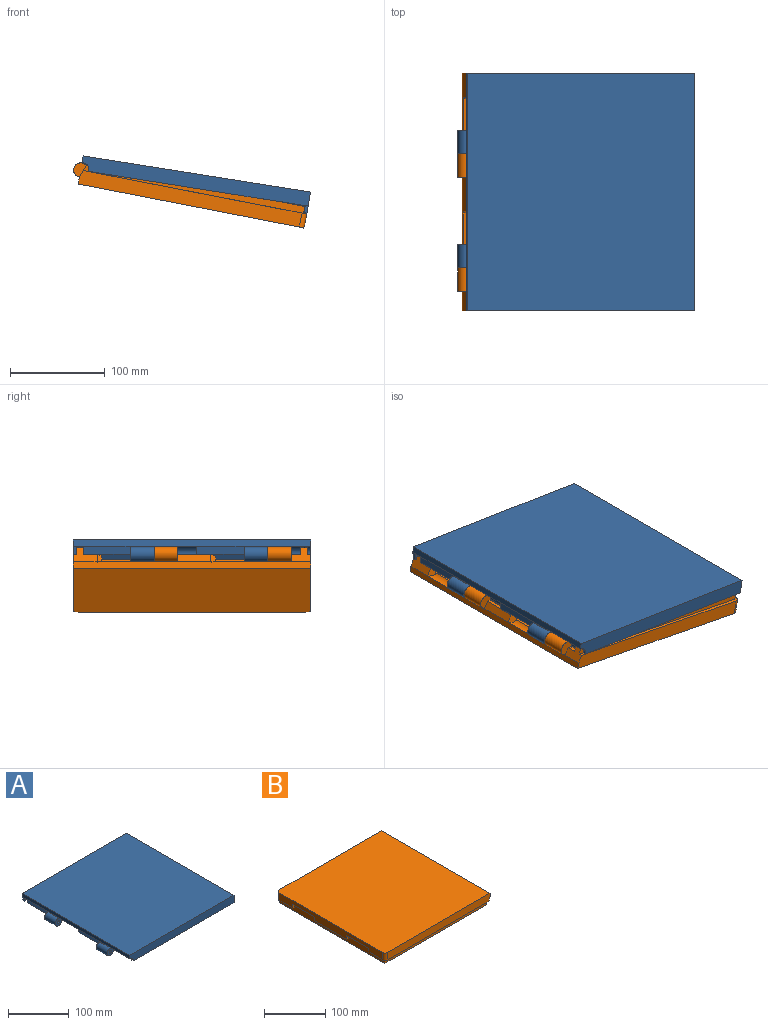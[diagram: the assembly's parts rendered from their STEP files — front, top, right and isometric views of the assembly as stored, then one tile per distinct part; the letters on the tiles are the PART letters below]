
ASSEMBLY  parts=2 mates=1
PART A: 51 faces, bbox 250x250x22.5 mm
  f0: plane 239.84x37.5mm, normal (0,0,-1), area 914.4mm2, adj f9,f12,f14,f18,f19,f49
  f1: plane 75x2.9mm, normal (0,0,-1), area 217.5mm2, adj f12,f18,f43,f50
  f2: plane 228.8x228.74mm, normal (0,0,-1), area 51620.4mm2, adj f3,f6,f8,f16,f19,f20,f21,f23
  f3: plane 70x8.5mm, normal (-0.95,0,-0.3), area 466.4mm2, adj f2,f10,f21,f23,f25,f30
  f4: plane 234x37.5mm, normal (0,0,-1), area 894.5mm2, adj f11,f12,f15,f18,f20,f44
  f5: plane 227.28x7.2mm, normal (0,0,-1), area 1636.4mm2, adj f8,f15,f16,f20
  f6: plane 231.09x7.5mm, normal (0,1,0), area 1724.1mm2, adj f2,f7,f16,f19
  f7: plane 230.97x7.2mm, normal (0,0,-1), area 1663mm2, adj f6,f14,f16,f19
  f8: plane 227.4x7.5mm, normal (0,-1,0), area 1681.2mm2, adj f2,f5,f16,f20
  f9: plane 242.5x15mm, normal (0,1,0), area 3626.2mm2, adj f0,f10,f12,f13,f19
  f10: plane 250x6.5mm, normal (-1,0,0), area 1625mm2, adj f3,f9,f11,f13,f19,f20,f31
  f11: plane 242.5x15mm, normal (0,-1,0), area 3580.8mm2, adj f4,f10,f12,f13,f20
  f12: plane 250x22.5mm, normal (1,0,0), area 4500mm2, adj f0,f1,f4,f9,f11,f13,f41,f43
  f13: plane 250x242.5mm, normal (0,0,1), area 60625mm2, adj f9,f10,f11,f12
  f14: plane 239.29x8mm, normal (0,-1,0), area 1789.7mm2, adj f0,f7,f16,f17,f18,f19
  f15: plane 235.6x8mm, normal (0,1,0), area 1746.8mm2, adj f4,f5,f16,f17,f18,f20
  f16: cylinder r=231.4mm len=243.2mm, axis (0,-1,0), area 1838mm2, adj f2,f5,f6,f7,f8,f14,f15,f17
  f17: plane 243.2x8.2mm, normal (0,0,-1), area 1995.4mm2, adj f14,f15,f16,f18
  f18: cylinder r=239.6mm len=243.2mm, axis (0,-1,0), area 1946mm2, adj f0,f1,f4,f14,f15,f17,f45,f48
  f19: plane 80x8.5mm, normal (-0.95,0,-0.3), area 498.8mm2, adj f0,f2,f6,f7,f9,f10,f14,f32
  f20: cylinder r=8.5mm len=50mm, axis (0,-1,0), area 601.4mm2, adj f2,f4,f5,f8,f10,f11,f15,f21
  f21: plane 8.5x8.5mm, normal (0,-1,0), area 12.4mm2, adj f2,f3,f20,f25
  f22: plane 5.4x5.4mm, normal (0,-1,0), area 22.7mm2, adj f24,f28,f29
  f23: plane 15x15mm, normal (0,1,0), area 143.7mm2, adj f2,f3,f25
  f24: cylinder r=2.7mm len=20mm, axis (0,1,0), area 312.8mm2, adj f22,f26,f27,f28,f29
  f25: cylinder r=7.5mm len=25mm, axis (0,1,0), area 948.8mm2, adj f2,f3,f21,f23,f26
  f26: plane 15x15mm, normal (0,-1,0), area 153.8mm2, adj f24,f25
  f27: plane 1.64x0.56mm, normal (0,-1,0), area 0.2mm2, adj f24,f28,f29
  f28: plane 15x1.64mm, normal (-0.95,0,-0.3), area 25.8mm2, adj f22,f24,f27,f29
  f29: plane 15x0.04mm, normal (0,0,-1), area 0.7mm2, adj f22,f24,f27,f28
  f30: plane 8.5x8.5mm, normal (0,1,0), area 45.5mm2, adj f2,f3,f31
  f31: cylinder r=8.5mm len=50mm, axis (0,-1,0), area 667.6mm2, adj f2,f10,f30,f32
  f32: plane 8.5x8.5mm, normal (0,-1,0), area 12.4mm2, adj f2,f19,f31,f36
  f33: plane 5.4x5.4mm, normal (0,-1,0), area 22.7mm2, adj f35,f39,f40
  f34: plane 15x15mm, normal (0,1,0), area 143.7mm2, adj f2,f19,f36
  f35: cylinder r=2.7mm len=20mm, axis (0,1,0), area 312.8mm2, adj f33,f37,f38,f39,f40
  f36: cylinder r=7.5mm len=25mm, axis (0,1,0), area 948.8mm2, adj f2,f19,f32,f34,f37
  f37: plane 15x15mm, normal (0,-1,0), area 153.8mm2, adj f35,f36
  f38: plane 1.64x0.56mm, normal (0,-1,0), area 0.2mm2, adj f35,f39,f40
  f39: plane 15x1.64mm, normal (-0.95,0,-0.3), area 25.8mm2, adj f33,f35,f38,f40
  f40: plane 15x0.04mm, normal (0,0,-1), area 0.7mm2, adj f33,f35,f38,f39
  f41: plane 50x3.03mm, normal (0,0,-1), area 151.7mm2, adj f12,f42,f43,f44
  f42: plane 50x7.5mm, normal (-1,0,0), area 375mm2, adj f41,f43,f44,f45
  f43: plane 7.5x3.03mm, normal (0,1,0), area 22.8mm2, adj f1,f12,f41,f42,f45
  f44: plane 7.5x3.03mm, normal (0,-1,0), area 22.8mm2, adj f4,f12,f41,f42,f45
  f45: plane 50x0.13mm, normal (0,0,1), area 6.7mm2, adj f18,f42,f43,f44
  f46: plane 50x3.03mm, normal (0,0,-1), area 151.7mm2, adj f12,f47,f49,f50
  f47: plane 50x7.5mm, normal (-1,0,0), area 375mm2, adj f46,f48,f49,f50
  f48: plane 50x0.13mm, normal (0,0,1), area 6.7mm2, adj f18,f47,f49,f50
  f49: plane 7.5x3.03mm, normal (0,1,0), area 22.8mm2, adj f0,f12,f46,f47,f48
  f50: plane 7.5x3.03mm, normal (0,-1,0), area 22.8mm2, adj f1,f12,f46,f47,f48
PART B: 51 faces, bbox 250x250x22.5 mm
  f0: plane 74x3.5mm, normal (0,0,-1), area 259mm2, adj f12,f15,f46,f48
  f1: plane 239.84x37mm, normal (0,0,-1), area 951.3mm2, adj f7,f9,f12,f15,f26,f43,f45
  f2: plane 236x8mm, normal (-1,0,0), area 1171.5mm2, adj f3,f5,f17,f19,f20,f21,f23,f24
  f3: plane 39.15x4.34mm, normal (0,0,-1), area 161mm2, adj f2,f4,f34,f38
  f4: plane 60x8.5mm, normal (0.95,0,-0.3), area 338.1mm2, adj f3,f13,f34,f35,f38,f39
  f5: plane 9.5x4.34mm, normal (0,0,-1), area 41.3mm2, adj f2,f6,f24,f30
  f6: plane 45x16mm, normal (0.95,0,-0.3), area 259.5mm2, adj f5,f8,f10,f11,f13,f16,f24,f27
  f7: plane 237.5x15mm, normal (0,1,0), area 3551.2mm2, adj f1,f13,f14,f26,f43
  f8: plane 237.5x15mm, normal (0,-1,0), area 3551.2mm2, adj f6,f11,f13,f14,f44
  f9: plane 236.34x7.5mm, normal (0,1,0), area 1763.8mm2, adj f1,f10,f15,f26
  f10: plane 243x234mm, normal (0,0,-1), area 4879mm2, adj f6,f9,f15,f16,f22,f23,f24,f26
  f11: plane 239.84x37mm, normal (0,0,-1), area 951.3mm2, adj f6,f8,f12,f15,f16,f44,f49
  f12: plane 240x15mm, normal (-1,0,0), area 2824.8mm2, adj f0,f1,f11,f14,f43,f44,f45,f46
  f13: plane 250x6.5mm, normal (1,0,0), area 1625mm2, adj f4,f6,f7,f8,f14,f26,f28,f36
  f14: plane 250x242.5mm, normal (0,0,1), area 60614.3mm2, adj f7,f8,f12,f13,f43,f44
  f15: plane 243x15.1mm, normal (-1,0,0), area 2597.7mm2, adj f0,f1,f9,f10,f11,f16,f45,f46
  f16: plane 236.34x7.5mm, normal (0,-1,0), area 1763.8mm2, adj f6,f10,f11,f15
  f17: plane 228.5x1mm, normal (0,-1,0), area 228.5mm2, adj f2,f18,f20,f21
  f18: plane 236x1mm, normal (1,0,0), area 236mm2, adj f17,f19,f20,f21
  f19: plane 228.5x1mm, normal (0,1,0), area 228.5mm2, adj f2,f18,f20,f21
  f20: plane 236x228.5mm, normal (0,0,-1), area 53926mm2, adj f2,f17,f18,f19
  f21: plane 236x228.5mm, normal (0,0,1), area 2401mm2, adj f2,f17,f18,f19,f22,f23,f24
  f22: plane 229x14.5mm, normal (1,0,0), area 3320.5mm2, adj f10,f21,f23,f24
  f23: plane 229.34x14.5mm, normal (0,-1,0), area 3286.3mm2, adj f2,f10,f21,f22,f25,f26
  f24: plane 229.34x14.5mm, normal (0,1,0), area 3286.3mm2, adj f2,f5,f6,f10,f21,f22
  f25: plane 18.65x4.34mm, normal (0,0,-1), area 72mm2, adj f2,f23,f26,f42
  f26: plane 25x16mm, normal (0.95,0,-0.3), area 277.6mm2, adj f1,f7,f9,f10,f13,f23,f25,f42
  f27: plane 16x15mm, normal (0,1,0), area 165.5mm2, adj f2,f6,f28,f31,f32
  f28: cylinder r=8.5mm len=60mm, axis (0,1,0), area 467.2mm2, adj f2,f13,f27,f29,f34
  f29: plane 3.14x0.98mm, normal (0,-1,0), area 1mm2, adj f2,f28,f34
  f30: plane 15x15mm, normal (0,-1,0), area 144.6mm2, adj f2,f5,f6,f31
  f31: cylinder r=7.5mm len=25mm, axis (0,-1,0), area 960.3mm2, adj f2,f6,f27,f30
  f32: cylinder r=2.5mm len=15mm, axis (0,-1,0), area 235.6mm2, adj f27,f33
  f33: plane 5x5mm, normal (0,1,0), area 19.6mm2, adj f32
  f34: plane 8.5x7mm, normal (0.67,-0.71,-0.21), area 55.9mm2, adj f2,f3,f4,f28,f29
  f35: plane 16x15mm, normal (0,1,0), area 165.5mm2, adj f2,f4,f36,f39,f40
  f36: cylinder r=8.5mm len=60mm, axis (0,1,0), area 467.2mm2, adj f2,f13,f35,f37,f42
  f37: plane 3.14x0.98mm, normal (0,-1,0), area 1mm2, adj f2,f36,f42
  f38: plane 15x15mm, normal (0,-1,0), area 144.6mm2, adj f2,f3,f4,f39
  f39: cylinder r=7.5mm len=25mm, axis (0,-1,0), area 960.3mm2, adj f2,f4,f35,f38
  f40: cylinder r=2.5mm len=15mm, axis (0,-1,0), area 235.6mm2, adj f35,f41
  f41: plane 5x5mm, normal (0,1,0), area 19.6mm2, adj f40
  f42: plane 8.5x7mm, normal (0.67,-0.71,-0.21), area 55.9mm2, adj f2,f25,f26,f36,f37
  f43: cylinder r=5mm len=15mm, axis (0,0,1), area 117.8mm2, adj f1,f7,f12,f14
  f44: cylinder r=5mm len=15mm, axis (0,0,-1), area 117.8mm2, adj f8,f11,f12,f14
  f45: plane 7.6x3.5mm, normal (0,-1,0), area 26.6mm2, adj f1,f12,f15,f47
  f46: plane 7.6x3.5mm, normal (0,1,0), area 26.6mm2, adj f0,f12,f15,f47
  f47: plane 51x3.5mm, normal (0,0,-1), area 178.5mm2, adj f12,f15,f45,f46
  f48: plane 7.6x3.5mm, normal (0,-1,0), area 26.6mm2, adj f0,f12,f15,f50
  f49: plane 7.6x3.5mm, normal (0,1,0), area 26.6mm2, adj f11,f12,f15,f50
  f50: plane 51x3.5mm, normal (0,0,-1), area 178.5mm2, adj f12,f15,f48,f49
PLACE A rot(axis=(0,1,0),9deg) t=(-6.83,64.97,4.45)mm
PLACE B rot(axis=(0,-1,0),169deg) t=(-6.83,64.97,4.45)mm
MATE cylindrical B.f28 <-> A.f20  axis (0,1,0) through (-6.83,-125.03,4.45)mm
